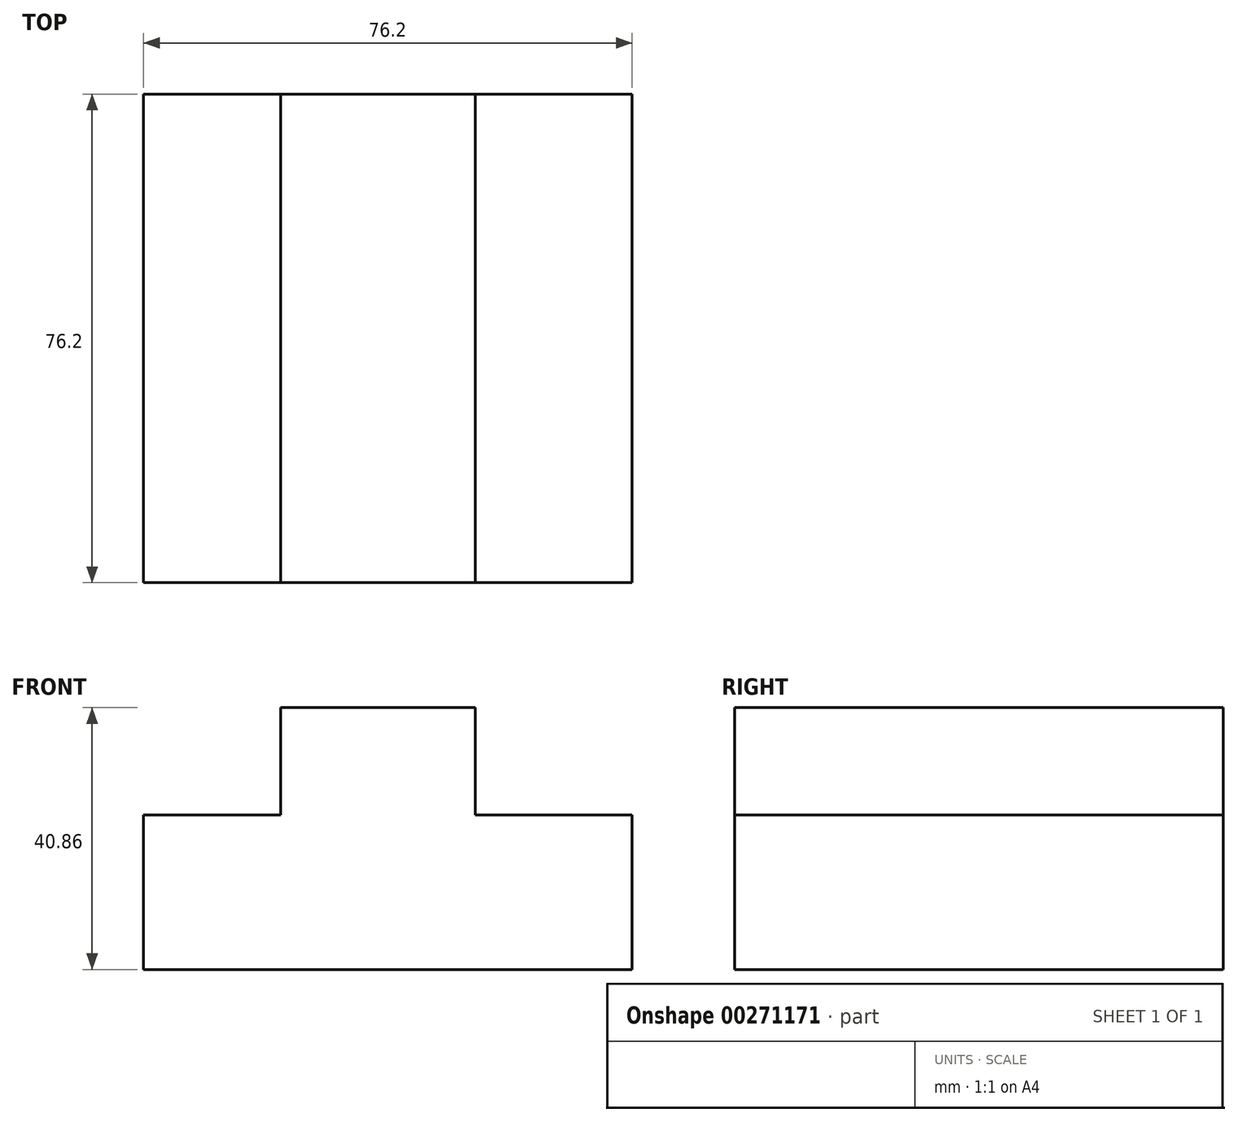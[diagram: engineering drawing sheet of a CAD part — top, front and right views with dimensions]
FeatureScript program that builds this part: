
annotation { "Feature Type Name" : "Feature", "Feature Type Description" : "" }
export const myFeature = defineFeature(function(context is Context, id is Id, definition is map)
    precondition{}
    {
        {
            var Q0;
            Q0=qCreatedBy(makeId("Front.planeOp"),FACE);
            var sketch = newSketch(context, id + "F0", { "sketchPlane" : qUnion([Q0])});
            skLineSegment(sketch, "E0", {"start": v(0, 0) * mm, "end": v(-76.2, 0) * mm});
            skLineSegment(sketch, "E1", {"start": v(-76.2, 0) * mm, "end": v(-76.2, 24.13) * mm});
            skLineSegment(sketch, "E2", {"start": v(-76.2, 24.13) * mm, "end": v(-54.8, 24.13) * mm});
            skLineSegment(sketch, "E3", {"start": v(-54.8, 24.13) * mm, "end": v(-54.8, 40.86) * mm});
            skLineSegment(sketch, "E4", {"start": v(-54.8, 40.86) * mm, "end": v(-24.44, 40.86) * mm});
            skLineSegment(sketch, "E5", {"start": v(-24.44, 40.86) * mm, "end": v(-24.44, 24.13) * mm});
            skLineSegment(sketch, "E6", {"start": v(-24.44, 24.13) * mm, "end": v(0, 24.13) * mm});
            skLineSegment(sketch, "E7", {"start": v(0, 24.13) * mm, "end": v(0, 0) * mm});
            skSolve(sketch);
        }
        {
            var Q0;
            Q0 = qSketchRegion(id + "F0", true);
            extrude(context, id + "F1", {"entities" : qUnion([Q0]), "depth" : 76.2 * mm});
        }
    });
